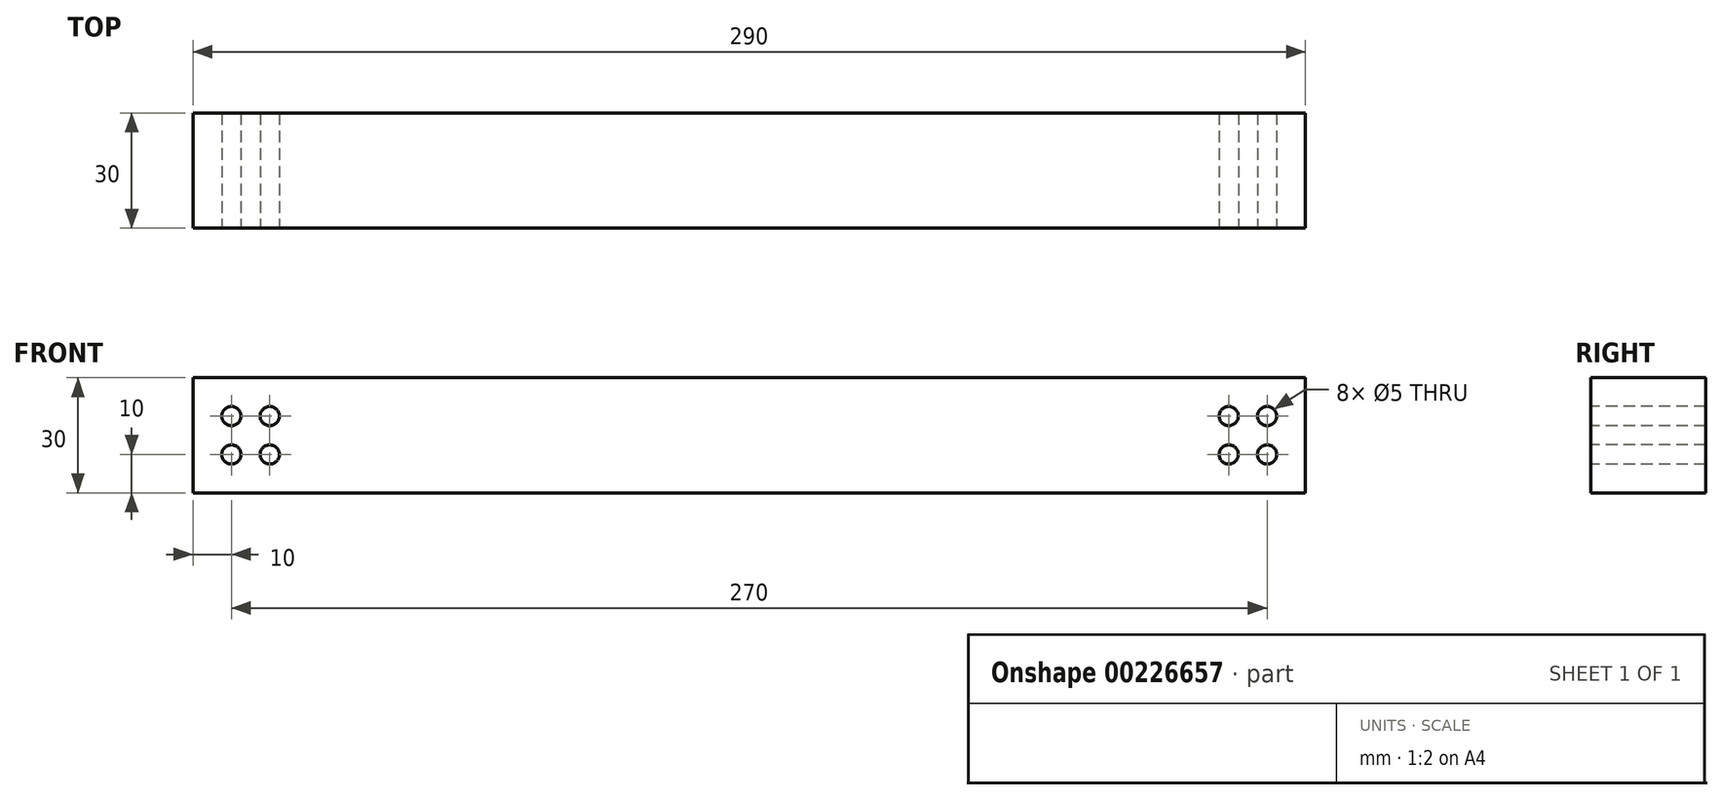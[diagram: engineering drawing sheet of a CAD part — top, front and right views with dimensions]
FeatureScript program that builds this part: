
annotation { "Feature Type Name" : "Feature", "Feature Type Description" : "" }
export const myFeature = defineFeature(function(context is Context, id is Id, definition is map)
    precondition{}
    {
        {
            var Q0;
            Q0=qCreatedBy(makeId("Front.planeOp"),FACE);
            var sketch = newSketch(context, id + "F0", { "sketchPlane" : qUnion([Q0])});
            skLineSegment(sketch, "E0.bottom", {"start": v(-145, 15) * mm, "end": v(145, 15) * mm});
            skLineSegment(sketch, "E0.top", {"start": v(-145, -15) * mm, "end": v(145, -15) * mm});
            skLineSegment(sketch, "E0.left", {"start": v(-145, 15) * mm, "end": v(-145, -15) * mm});
            skLineSegment(sketch, "E0.right", {"start": v(145, 15) * mm, "end": v(145, -15) * mm});
            skLineSegment(sketch, "E1", {"start": v(0, 15) * mm, "end": v(0, -15) * mm, "construction": true});
            skLineSegment(sketch, "E2", {"start": v(-145, 0) * mm, "end": v(145, 0) * mm, "construction": true});
            skSolve(sketch);
        }
        {
            var Q0;
            Q0=makeQuery(id+"F0.imprint","IMPRINT",FACE,{"disambiguationData":[TD([[makeQuery(id+"F0.imprint","IMPRINT",EDGE,{"derivedFrom":sQuery(id+"F0.wireOp",EDGE,"E0.bottom")}),-1.0]])]});
            extrude(context, id + "F1", {"entities" : qUnion([Q0]), "endBound" : BoundingType.SYMMETRIC, "depth" : 30 * mm});
        }
        {
            var Q0;
            Q0=makeQuery(id+"F1.opExtrude","CAP_FACE",FACE,{"disambiguationData":[OSD([sQuery(id+"F0.wireOp",EDGE,"E0.bottom"),sQuery(id+"F0.wireOp",EDGE,"E0.top"),sQuery(id+"F0.wireOp",EDGE,"E0.left"),sQuery(id+"F0.wireOp",EDGE,"E0.right")])],"isStart":false});
            var sketch = newSketch(context, id + "F2", { "sketchPlane" : qUnion([Q0])});
            skPoint(sketch, "E3", {"position": v(-135, 5) * mm});
            skPoint(sketch, "E4", {"position": v(-125, -5) * mm});
            skPoint(sketch, "E5", {"position": v(-125, 5) * mm});
            skPoint(sketch, "E6", {"position": v(-135, -5) * mm});
            skPoint(sketch, "E7", {"position": v(125, 5) * mm});
            skPoint(sketch, "E8", {"position": v(135, 5) * mm});
            skPoint(sketch, "E9", {"position": v(125, -5) * mm});
            skPoint(sketch, "E10", {"position": v(135, -5) * mm});
            skSolve(sketch);
        }
        {
            var Q0;
            Q0=sQuery(id+"F2.wireOp",VERTEX,"E3");
            var Q1;
            Q1=sQuery(id+"F2.wireOp",VERTEX,"E6");
            var Q2;
            Q2=sQuery(id+"F2.wireOp",VERTEX,"E5");
            var Q3;
            Q3=sQuery(id+"F2.wireOp",VERTEX,"E4");
            var Q4;
            Q4=sQuery(id+"F2.wireOp",VERTEX,"E7");
            var Q5;
            Q5=sQuery(id+"F2.wireOp",VERTEX,"E9");
            var Q6;
            Q6=sQuery(id+"F2.wireOp",VERTEX,"E8");
            var Q7;
            Q7=sQuery(id+"F2.wireOp",VERTEX,"E10");
            var Q8;
            Q8=sQuery(id+"F2.wireOp",VERTEX,"7351444d-8868-4ae4-b58a-4751c27e0c9d");
            var Q9;
            Q9=sQuery(id+"F2.wireOp",VERTEX,"88f961ae-2465-4a6d-8427-ac9aa31ac5c2");
            var Q10;
            Q10=sQuery(id+"F2.wireOp",VERTEX,"dda9f3fc-00b3-4cc7-9425-bd961587f18f");
            var Q11;
            Q11=sQuery(id+"F2.wireOp",VERTEX,"5ca1f574-1488-4a9d-8cb8-c2e72dfb782c");
            var Q12;
            Q12=sQuery(id+"F2.wireOp",VERTEX,"f418ea0f-289d-4ded-85b0-ffbec062acae");
            var Q13;
            Q13=sQuery(id+"F2.wireOp",VERTEX,"85ee84fe-6725-4aa5-bf82-01b79e210c9d");
            var Q14;
            Q14=sQuery(id+"F2.wireOp",VERTEX,"5cbbfdf9-609c-483d-817f-3dc098588def");
            var Q15;
            Q15=sQuery(id+"F2.wireOp",VERTEX,"11ccb516-69b1-43ca-91d6-993ba786c0c5");
            var Q16;
            Q16=makeQuery(id+"F1.opExtrude","SWEPT_BODY",BODY,{"disambiguationData":[OSD([sQuery(id+"F0.wireOp",EDGE,"E0.bottom"),sQuery(id+"F0.wireOp",EDGE,"E0.top"),sQuery(id+"F0.wireOp",EDGE,"E0.left"),sQuery(id+"F0.wireOp",EDGE,"E0.right")])]});
            hole(context, id + "F3", {"style" : HoleStyle.SIMPLE, "endStyle" : HoleEndStyle.THROUGH, "holeDiameter" : 5 * mm, "locations" : qUnion([Q0, Q1, Q2, Q3, Q4, Q5, Q6, Q7, Q8, Q9, Q10, Q11, Q12, Q13, Q14, Q15]), "scope" : qUnion([Q16]), "isTappedThrough" : true});
        }
    });
